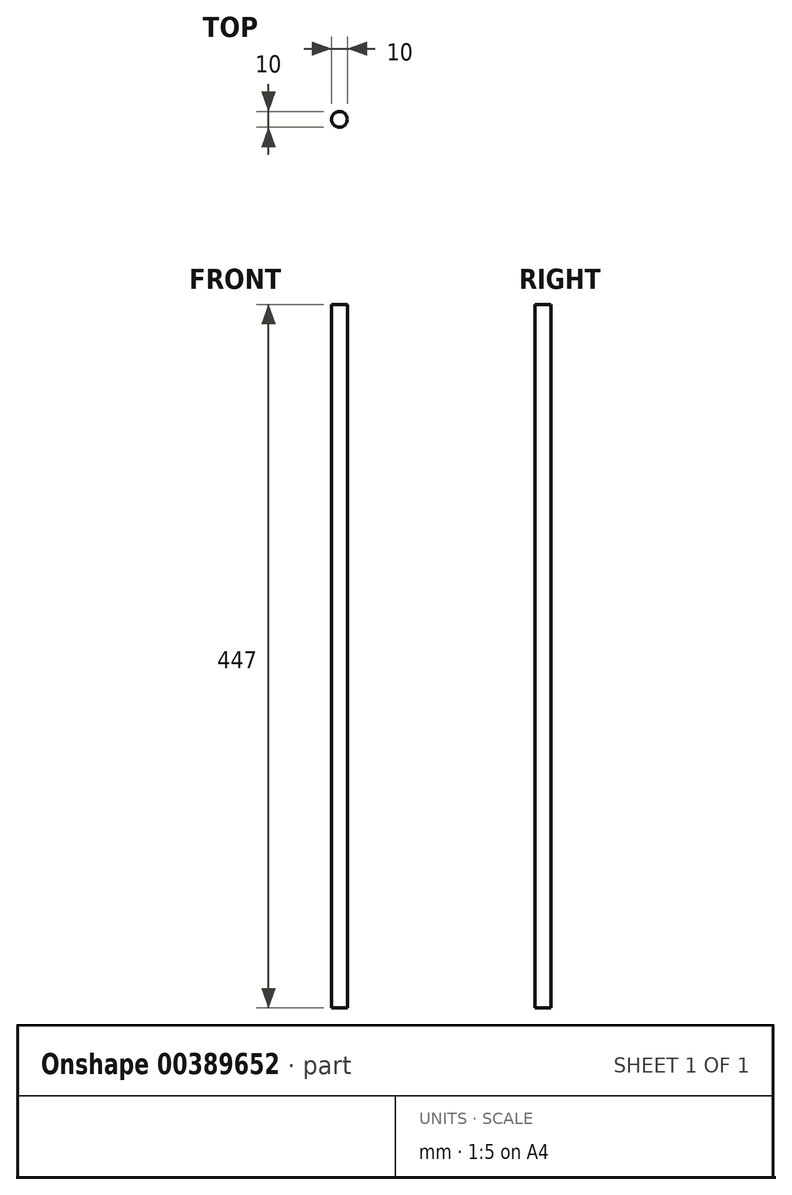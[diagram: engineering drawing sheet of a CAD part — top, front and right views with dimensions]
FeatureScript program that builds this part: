
annotation { "Feature Type Name" : "Feature", "Feature Type Description" : "" }
export const myFeature = defineFeature(function(context is Context, id is Id, definition is map)
    precondition{}
    {
        {
            var Q0;
            Q0=qCreatedBy(makeId("Top.planeOp"),FACE);
            var sketch = newSketch(context, id + "F0", { "sketchPlane" : qUnion([Q0])});
            skCircle(sketch, "E0", {"center": v(0, 0) * mm, "radius": 5 * mm});
            skSolve(sketch);
        }
        {
            var Q0;
            Q0=qSketchRegion(id+"F0",true);
            extrude(context, id + "F1", {"entities" : qUnion([Q0]), "depth" : 447 * mm});
        }
    });
